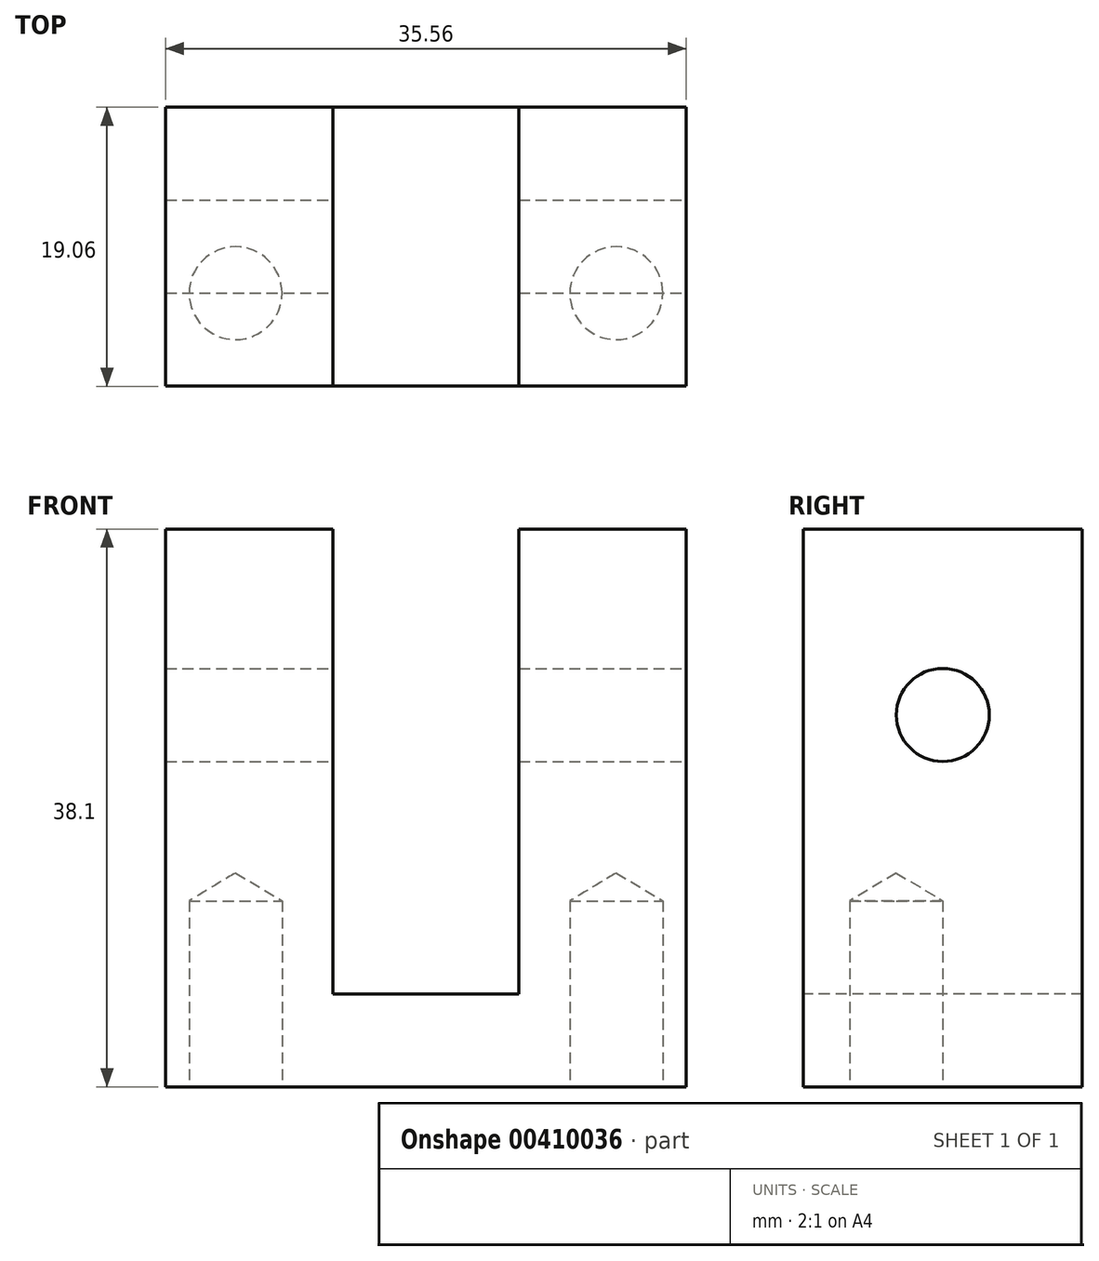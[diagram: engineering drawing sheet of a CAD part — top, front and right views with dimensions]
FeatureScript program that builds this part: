
annotation { "Feature Type Name" : "Feature", "Feature Type Description" : "" }
export const myFeature = defineFeature(function(context is Context, id is Id, definition is map)
    precondition{}
    {
        {
            var Q0;
            Q0=qCreatedBy(makeId("Right.planeOp"),FACE);
            var sketch = newSketch(context, id + "F0", { "sketchPlane" : qUnion([Q0])});
            skLineSegment(sketch, "E0.bottom", {"start": v(9.53, 19.05) * mm, "end": v(-9.52, 19.05) * mm});
            skLineSegment(sketch, "E0.top", {"start": v(9.53, -19.05) * mm, "end": v(-9.53, -19.05) * mm});
            skLineSegment(sketch, "E0.left", {"start": v(9.53, 19.05) * mm, "end": v(9.53, -19.05) * mm});
            skLineSegment(sketch, "E0.right", {"start": v(-9.52, 19.05) * mm, "end": v(-9.53, -19.05) * mm});
            skPoint(sketch, "E0.middle", {"position": v(0, 0) * mm});
            skSolve(sketch);
        }
        {
            var Q0;
            Q0 = qSketchRegion(id + "F0", true);
            extrude(context, id + "F1", {"entities" : qUnion([Q0]), "depth" : 35.56 * mm});
        }
        {
            var Q0;
            Q0=makeQuery(id+"F1.opExtrude","SWEPT_FACE",FACE,{"disambiguationData":[OSD([sQuery(id+"F0.wireOp",EDGE,"E0.right")])]});
            var sketch = newSketch(context, id + "F2", { "sketchPlane" : qUnion([Q0])});
            skLineSegment(sketch, "E1.bottom", {"start": v(11.43, 40.27) * mm, "end": v(24.13, 40.27) * mm});
            skLineSegment(sketch, "E1.top", {"start": v(11.43, -12.7) * mm, "end": v(24.13, -12.7) * mm});
            skLineSegment(sketch, "E1.left", {"start": v(11.43, 40.27) * mm, "end": v(11.43, -12.7) * mm});
            skLineSegment(sketch, "E1.right", {"start": v(24.13, 40.27) * mm, "end": v(24.13, -12.7) * mm});
            skSolve(sketch);
        }
        {
            var Q0;
            Q0 = qSketchRegion(id + "F2", true);
            extrude(context, id + "F3", {"entities" : qUnion([Q0]), "operationType" : NewBodyOperationType.REMOVE, "oppositeDirection" : true, "depth" : 25.4 * mm});
        }
        {
            var Q0;
            Q0=makeQuery(id+"F1.opExtrude","CAP_FACE",FACE,{"disambiguationData":[OSD([sQuery(id+"F0.wireOp",EDGE,"E0.bottom"),sQuery(id+"F0.wireOp",EDGE,"E0.top"),sQuery(id+"F0.wireOp",EDGE,"E0.left"),sQuery(id+"F0.wireOp",EDGE,"E0.right")])],"isStart":false});
            var sketch = newSketch(context, id + "F4", { "sketchPlane" : qUnion([Q0])});
            skCircle(sketch, "E2", {"center": v(0, 6.35) * mm, "radius": 3.17 * mm});
            skSolve(sketch);
        }
        {
            var Q0;
            Q0 = qSketchRegion(id + "F4", true);
            extrude(context, id + "F5", {"entities" : qUnion([Q0]), "operationType" : NewBodyOperationType.REMOVE, "endBound" : BoundingType.THROUGH_ALL, "oppositeDirection" : true, "depth" : 25.4 * mm});
        }
        {
            var Q0;
            Q0=makeQuery(id+"F1.opExtrude","SWEPT_FACE",FACE,{"disambiguationData":[OSD([sQuery(id+"F0.wireOp",EDGE,"E0.top")])]});
            var sketch = newSketch(context, id + "F6", { "sketchPlane" : qUnion([Q0])});
            skPoint(sketch, "E3", {"position": v(4.78, 3.18) * mm});
            skPoint(sketch, "E4", {"position": v(30.78, 3.18) * mm});
            skSolve(sketch);
        }
        {
            var Q0;
            Q0=sQuery(id+"F6.wireOp",VERTEX,"E3");
            var Q1;
            Q1=sQuery(id+"F6.wireOp",VERTEX,"E4");
            var Q2;
            Q2=makeQuery(id+"F1.opExtrude","SWEPT_BODY",BODY,{"disambiguationData":[OSD([sQuery(id+"F0.wireOp",EDGE,"E0.bottom"),sQuery(id+"F0.wireOp",EDGE,"E0.top"),sQuery(id+"F0.wireOp",EDGE,"E0.left"),sQuery(id+"F0.wireOp",EDGE,"E0.right")])]});
            hole(context, id + "F7", {"style" : HoleStyle.SIMPLE, "endStyle" : HoleEndStyle.BLIND, "holeDiameter" : 6.35 * mm, "holeDepth" : 12.7 * mm, "isTappedThrough" : true, "tappedDepth" : 12.7 * mm, "tapClearance" : 3, "locations" : qUnion([Q0, Q1]), "scope" : qUnion([Q2])});
        }
    });
